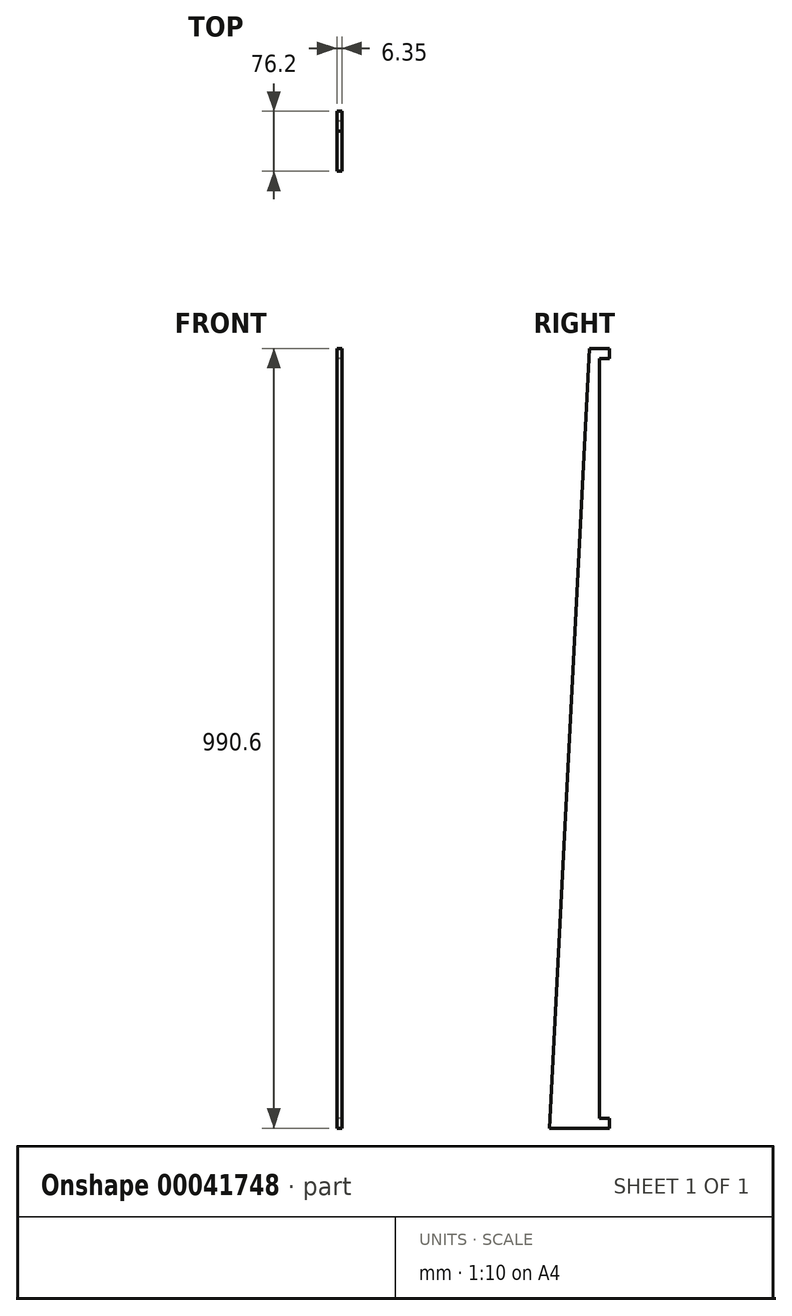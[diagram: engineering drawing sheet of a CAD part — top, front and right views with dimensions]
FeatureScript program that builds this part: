
annotation { "Feature Type Name" : "Feature", "Feature Type Description" : "" }
export const myFeature = defineFeature(function(context is Context, id is Id, definition is map)
    precondition{}
    {
        {
            var Q0;
            Q0=qCreatedBy(makeId("Right.planeOp"),FACE);
            var sketch = newSketch(context, id + "F0", { "sketchPlane" : qUnion([Q0])});
            skLineSegment(sketch, "E0", {"start": v(0, 120.21) * mm, "end": v(0, 107.51) * mm});
            skLineSegment(sketch, "E1", {"start": v(0, 107.51) * mm, "end": v(-12.7, 107.51) * mm});
            skLineSegment(sketch, "E2", {"start": v(-12.7, 107.51) * mm, "end": v(-12.7, -857.69) * mm});
            skLineSegment(sketch, "E3", {"start": v(-12.7, -857.69) * mm, "end": v(0, -857.69) * mm});
            skLineSegment(sketch, "E4", {"start": v(0, -857.69) * mm, "end": v(0, -870.39) * mm});
            skLineSegment(sketch, "E5", {"start": v(0, -870.39) * mm, "end": v(-76.2, -870.39) * mm});
            skLineSegment(sketch, "E6", {"start": v(-76.2, -870.39) * mm, "end": v(-25.4, 120.21) * mm});
            skLineSegment(sketch, "E7", {"start": v(-25.4, 120.21) * mm, "end": v(0, 120.21) * mm});
            skSolve(sketch);
        }
        {
            var Q0;
            Q0 = qSketchRegion(id + "F0", true);
            extrude(context, id + "F1", {"entities" : qUnion([Q0]), "depth" : 6.35 * mm});
        }
    });
